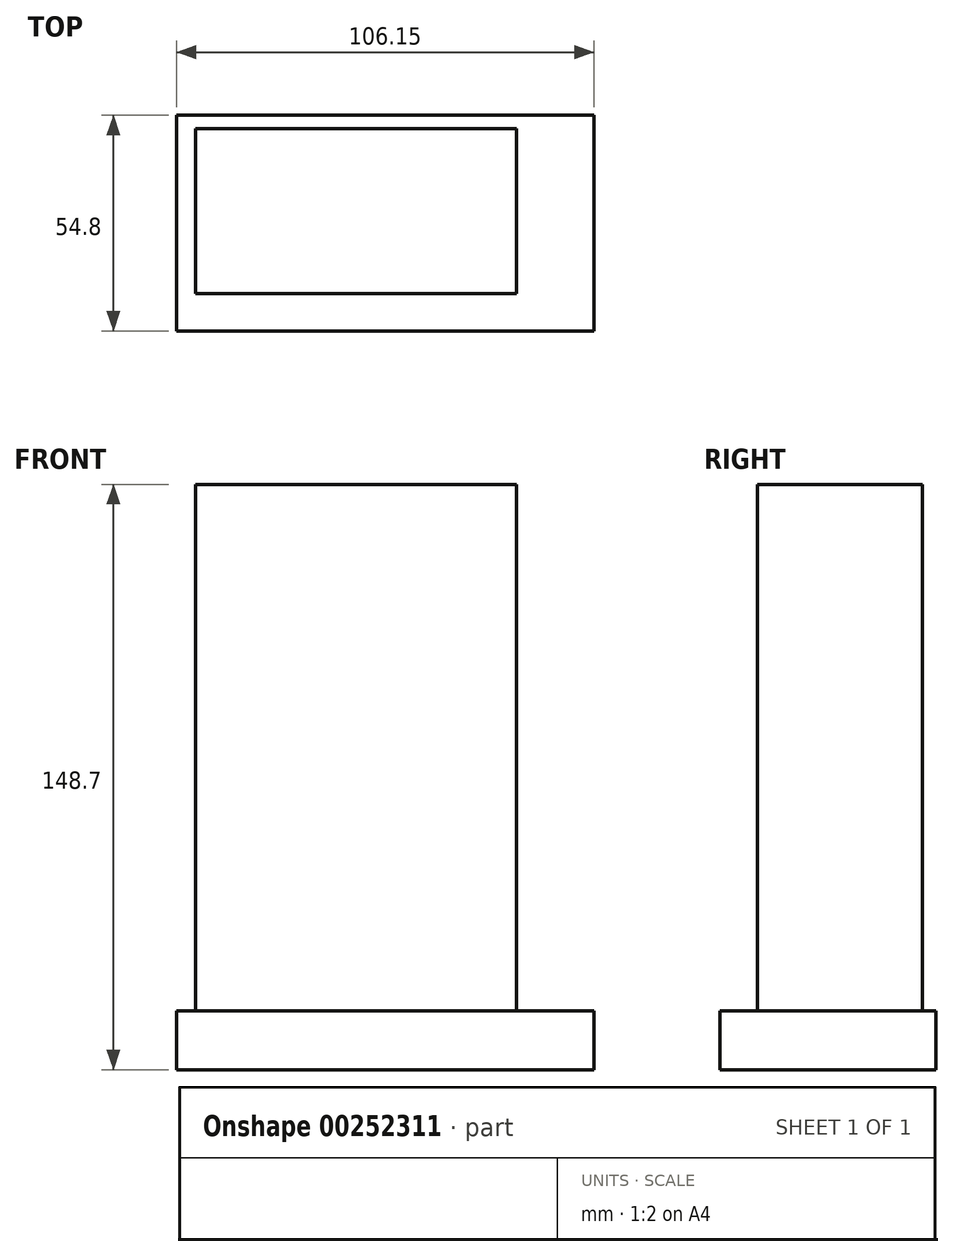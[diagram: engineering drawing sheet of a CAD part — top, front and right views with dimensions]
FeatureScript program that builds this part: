
annotation { "Feature Type Name" : "Feature", "Feature Type Description" : "" }
export const myFeature = defineFeature(function(context is Context, id is Id, definition is map)
    precondition{}
    {
        {
            var Q0;
            Q0=qCreatedBy(makeId("Top.planeOp"),FACE);
            var sketch = newSketch(context, id + "F0", { "sketchPlane" : qUnion([Q0])});
            skLineSegment(sketch, "E0.bottom", {"start": v(48.2, 27.4) * mm, "end": v(-57.95, 27.4) * mm});
            skLineSegment(sketch, "E0.top", {"start": v(48.2, -27.4) * mm, "end": v(-57.95, -27.4) * mm});
            skLineSegment(sketch, "E0.left", {"start": v(48.2, 27.4) * mm, "end": v(48.2, -27.4) * mm});
            skLineSegment(sketch, "E0.right", {"start": v(-57.95, 27.4) * mm, "end": v(-57.95, -27.4) * mm});
            skPoint(sketch, "E0.middle", {"position": v(-4.88, 0) * mm});
            skSolve(sketch);
        }
        {
            var Q0;
            Q0=makeQuery(id+"F0.imprint","IMPRINT",FACE,{"disambiguationData":[TD([[makeQuery(id+"F0.imprint","IMPRINT",EDGE,{"derivedFrom":sQuery(id+"F0.wireOp",EDGE,"E0.bottom")}),1.0]])]});
            extrude(context, id + "F1", {"entities" : qUnion([Q0]), "endBound" : BoundingType.SYMMETRIC, "depth" : 15 * mm});
        }
        {
            var Q0;
            Q0=makeQuery(id+"F1.opExtrude","CAP_FACE",FACE,{"disambiguationData":[OSD([sQuery(id+"F0.wireOp",EDGE,"E0.bottom"),sQuery(id+"F0.wireOp",EDGE,"E0.top"),sQuery(id+"F0.wireOp",EDGE,"E0.left"),sQuery(id+"F0.wireOp",EDGE,"E0.right")])],"isStart":false});
            var sketch = newSketch(context, id + "F2", { "sketchPlane" : qUnion([Q0])});
            skLineSegment(sketch, "E1.bottom", {"start": v(28.4, -17.93) * mm, "end": v(-53.07, -17.93) * mm});
            skLineSegment(sketch, "E1.top", {"start": v(28.4, 23.95) * mm, "end": v(-53.07, 23.95) * mm});
            skLineSegment(sketch, "E1.left", {"start": v(28.4, -17.93) * mm, "end": v(28.4, 23.95) * mm});
            skLineSegment(sketch, "E1.right", {"start": v(-53.07, -17.93) * mm, "end": v(-53.07, 23.95) * mm});
            skPoint(sketch, "E1.middle", {"position": v(-12.34, 3.01) * mm});
            skSolve(sketch);
        }
        {
            var Q0;
            Q0=makeQuery(id+"F2.imprint","IMPRINT",FACE,{"disambiguationData":[TD([[makeQuery(id+"F2.imprint","IMPRINT",EDGE,{"derivedFrom":sQuery(id+"F2.wireOp",EDGE,"E1.bottom")}),-1.0]])]});
            extrude(context, id + "F3", {"entities" : qUnion([Q0]), "operationType" : NewBodyOperationType.ADD, "depth" : 133.7 * mm});
        }
    });
